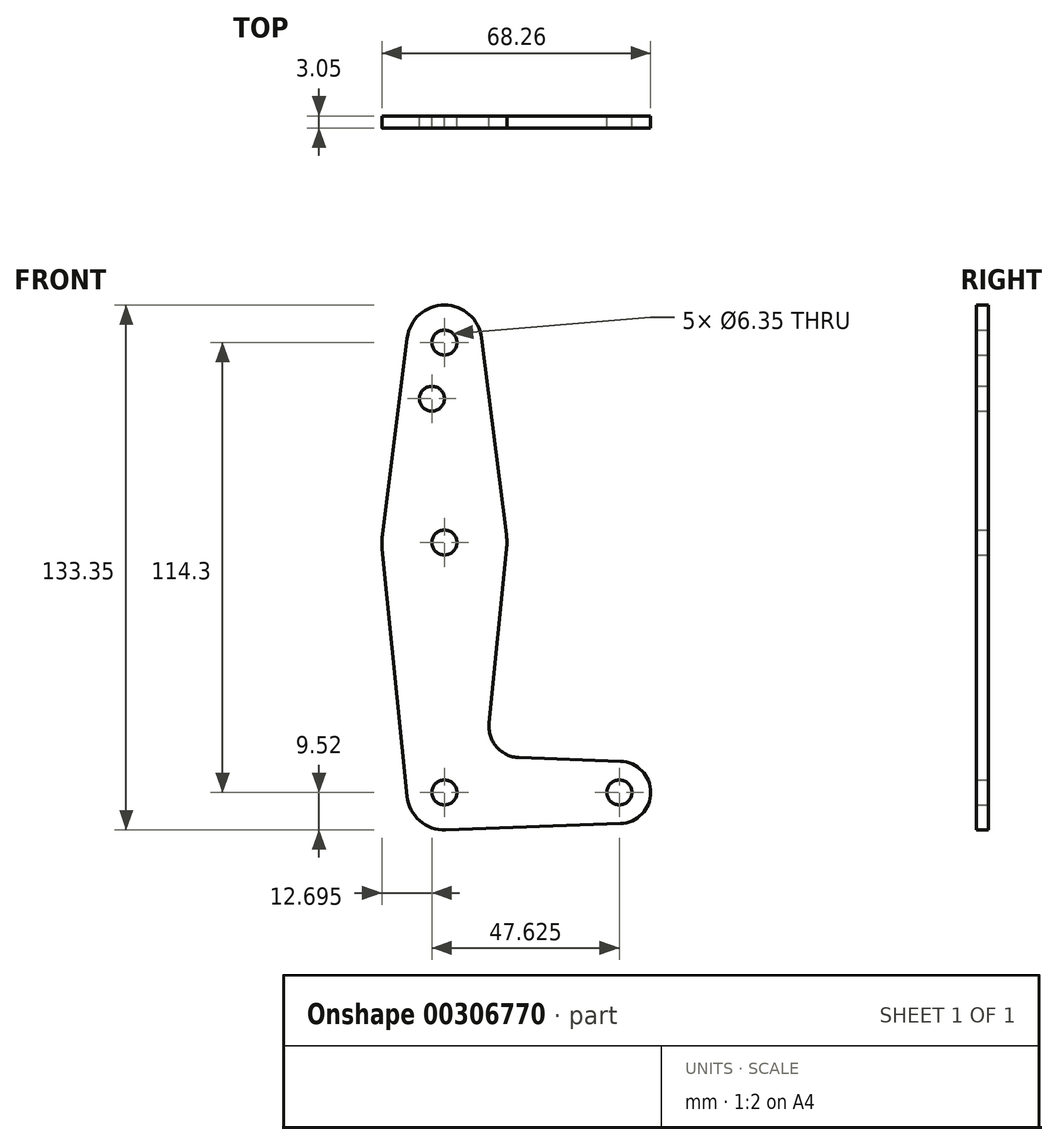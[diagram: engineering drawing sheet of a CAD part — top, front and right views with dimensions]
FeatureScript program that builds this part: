
annotation { "Feature Type Name" : "Feature", "Feature Type Description" : "" }
export const myFeature = defineFeature(function(context is Context, id is Id, definition is map)
    precondition{}
    {
        {
            var Q0;
            Q0=qCreatedBy(makeId("Front.planeOp"),FACE);
            var sketch = newSketch(context, id + "F0", { "sketchPlane" : qUnion([Q0])});
            skLineSegment(sketch, "E0", {"start": v(0, 0) * mm, "end": v(0, 114.3) * mm, "construction": true});
            skLineSegment(sketch, "E1", {"start": v(0, 0) * mm, "end": v(44.45, 0) * mm, "construction": true});
            skCircle(sketch, "E2", {"center": v(0, 114.3) * mm, "radius": 9.53 * mm});
            skCircle(sketch, "E3", {"center": v(0, 63.5) * mm, "radius": 15.88 * mm});
            skCircle(sketch, "E4", {"center": v(0, 0) * mm, "radius": 9.53 * mm});
            skCircle(sketch, "E5", {"center": v(44.45, 0) * mm, "radius": 7.94 * mm});
            skLineSegment(sketch, "E6", {"start": v(-9.45, 115.5) * mm, "end": v(-15.75, 65.48) * mm});
            skLineSegment(sketch, "E7", {"start": v(15.75, 65.48) * mm, "end": v(9.45, 115.5) * mm});
            skLineSegment(sketch, "E8", {"start": v(15.8, 61.91) * mm, "end": v(11.34, 17.6) * mm});
            skLineSegment(sketch, "E9", {"start": v(-15.8, 61.91) * mm, "end": v(-9.48, -0.95) * mm});
            skLineSegment(sketch, "E10", {"start": v(18.97, 8.85) * mm, "end": v(44.73, 7.93) * mm});
            skLineSegment(sketch, "E11", {"start": v(0.34, -9.52) * mm, "end": v(44.73, -7.93) * mm});
            skCircle(sketch, "E12", {"center": v(0, 114.3) * mm, "radius": 3.18 * mm});
            skCircle(sketch, "E13", {"center": v(-3.18, 100.03) * mm, "radius": 3.18 * mm});
            skCircle(sketch, "E14", {"center": v(0, 63.5) * mm, "radius": 3.18 * mm});
            skCircle(sketch, "E15", {"center": v(0, 0) * mm, "radius": 3.18 * mm});
            skCircle(sketch, "E16", {"center": v(44.45, 0) * mm, "radius": 3.18 * mm});
            skArc(sketch, "E17.filletArc", {"start": v(11.34, 17.6) * mm, "mid": v(13.26, 11.57) * mm, "end": v(18.97, 8.85) * mm});
            skSolve(sketch);
        }
        {
            var Q0;
            Q0 = qSketchRegion(id + "F0", true);
            extrude(context, id + "F1", {"entities" : qUnion([Q0]), "depth" : 3.05 * mm});
        }
    });
